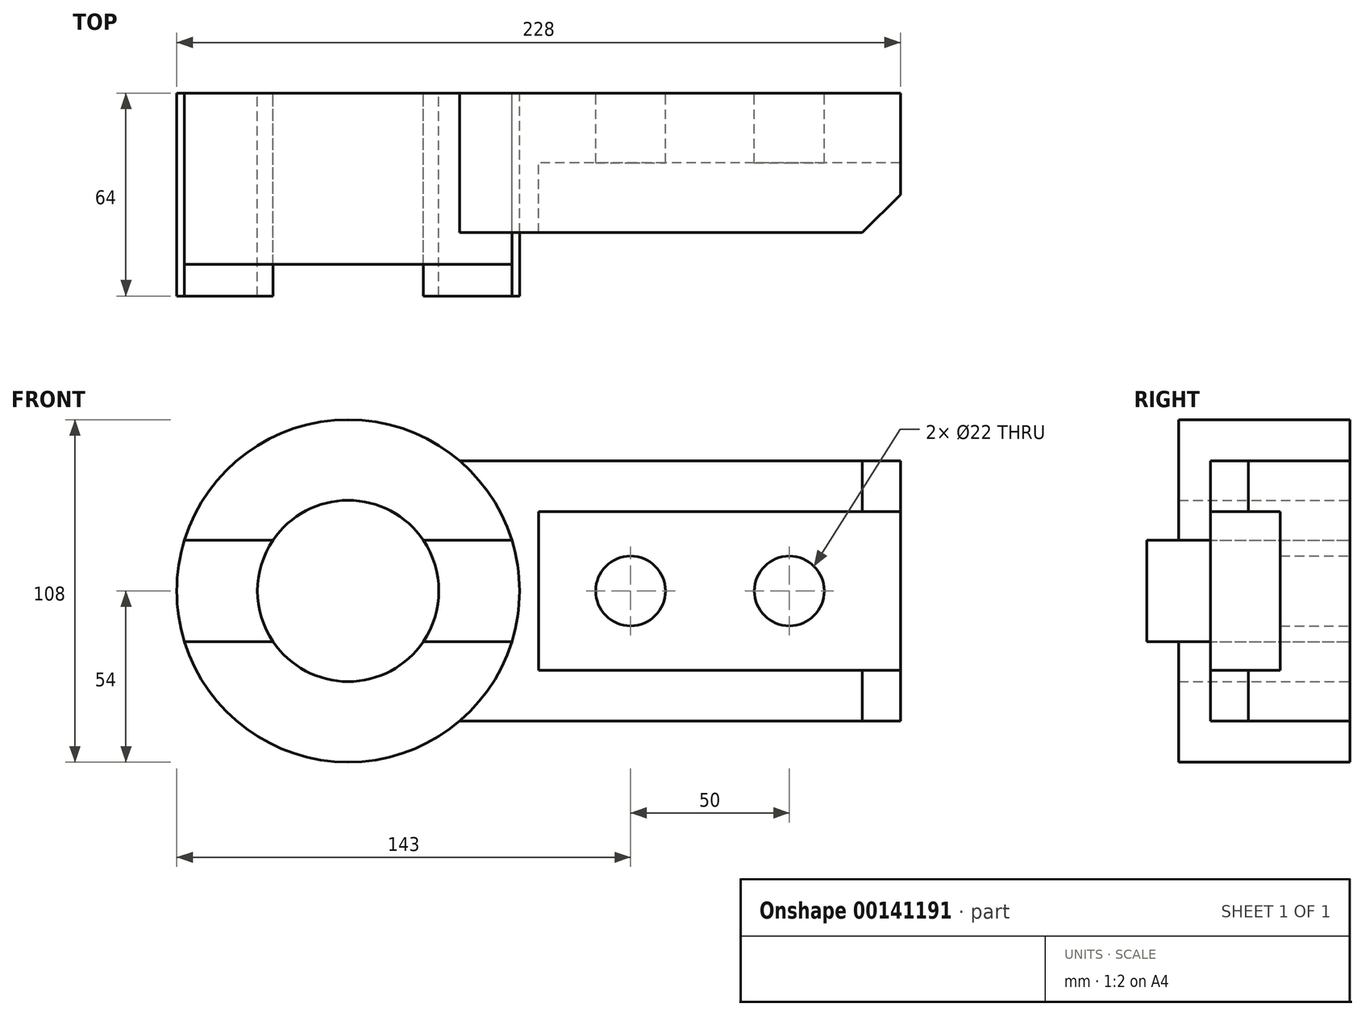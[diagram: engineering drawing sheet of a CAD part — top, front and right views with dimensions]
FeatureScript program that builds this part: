
annotation { "Feature Type Name" : "Feature", "Feature Type Description" : "" }
export const myFeature = defineFeature(function(context is Context, id is Id, definition is map)
    precondition{}
    {
        {
            var Q0;
            Q0=qCreatedBy(makeId("Front.planeOp"),FACE);
            var sketch = newSketch(context, id + "F0", { "sketchPlane" : qUnion([Q0])});
            skCircle(sketch, "E0", {"center": v(0, 0) * mm, "radius": 54 * mm});
            skLineSegment(sketch, "E1", {"start": v(35.14, 41) * mm, "end": v(174, 41) * mm});
            skLineSegment(sketch, "E2.MirrorCS", {"start": v(35.14, -41) * mm, "end": v(174, -41) * mm});
            skLineSegment(sketch, "E3", {"start": v(174, 41) * mm, "end": v(174, -41) * mm});
            skLineSegment(sketch, "E4", {"start": v(174, 25) * mm, "end": v(60, 25) * mm});
            skLineSegment(sketch, "E5.MirrorCS", {"start": v(174, -25) * mm, "end": v(60, -25) * mm});
            skLineSegment(sketch, "E6", {"start": v(60, 25) * mm, "end": v(60, -25) * mm});
            skCircle(sketch, "E7", {"center": v(89, 0) * mm, "radius": 11 * mm});
            skCircle(sketch, "E8", {"center": v(139, 0) * mm, "radius": 11 * mm});
            skCircle(sketch, "E9", {"center": v(0, 0) * mm, "radius": 28.57 * mm});
            skLineSegment(sketch, "E10", {"start": v(-51.58, 16) * mm, "end": v(-23.68, 16) * mm});
            skLineSegment(sketch, "E11", {"start": v(23.68, 16) * mm, "end": v(51.58, 16) * mm});
            skLineSegment(sketch, "E12.MirrorCS", {"start": v(-51.58, -16) * mm, "end": v(-23.68, -16) * mm});
            skLineSegment(sketch, "E13.MirrorCS", {"start": v(23.68, -16) * mm, "end": v(51.58, -16) * mm});
            skSolve(sketch);
        }
        {
            var Q0;
            {var subQ0=sQuery(id+"F0.wireOp",EDGE,"E10");Q0=makeQuery(id+"F0.imprint","IMPRINT",FACE,{"disambiguationData":[TD([[makeQuery(id+"F0.imprint","IMPRINT",EDGE,{"derivedFrom":subQ0}),1.0]])]});}
            var Q1;
            {var subQ0=sQuery(id+"F0.wireOp",EDGE,"E12.MirrorCS");Q1=makeQuery(id+"F0.imprint","IMPRINT",FACE,{"disambiguationData":[TD([[makeQuery(id+"F0.imprint","IMPRINT",EDGE,{"derivedFrom":subQ0}),-1.0]])]});}
            extrude(context, id + "F1", {"entities" : qUnion([Q0, Q1]), "depth" : 54 * mm});
        }
        {
            var Q0;
            {var subQ0=sQuery(id+"F0.wireOp",EDGE,"E10");Q0=makeQuery(id+"F0.imprint","IMPRINT",FACE,{"disambiguationData":[TD([[makeQuery(id+"F0.imprint","IMPRINT",EDGE,{"derivedFrom":subQ0}),-1.0]])]});}
            var Q1;
            {var subQ0=sQuery(id+"F0.wireOp",EDGE,"E11");Q1=makeQuery(id+"F0.imprint","IMPRINT",FACE,{"disambiguationData":[TD([[makeQuery(id+"F0.imprint","IMPRINT",EDGE,{"derivedFrom":subQ0}),-1.0]])]});}
            extrude(context, id + "F2", {"entities" : qUnion([Q0, Q1]), "depth" : 64 * mm});
        }
        {
            var Q0;
            {var subQ0=sQuery(id+"F0.wireOp",EDGE,"E1");Q0=makeQuery(id+"F0.imprint","IMPRINT",FACE,{"disambiguationData":[TD([[makeQuery(id+"F0.imprint","IMPRINT",EDGE,{"derivedFrom":subQ0}),-1.0]])]});}
            extrude(context, id + "F3", {"entities" : qUnion([Q0]), "depth" : 44 * mm});
        }
        {
            var Q0;
            {var subQ1=sQuery(id+"F0.wireOp",EDGE,"E4");Q0=makeQuery(id+"F0.imprint","IMPRINT",FACE,{"disambiguationData":[TD([[makeQuery(id+"F0.imprint","IMPRINT",EDGE,{"derivedFrom":subQ1}),1.0]])]});}
            extrude(context, id + "F4", {"entities" : qUnion([Q0]), "operationType" : NewBodyOperationType.ADD, "depth" : 22 * mm});
        }
        {
            var Q0;
            Q0=makeQuery(id+"F3.opExtrude","SWEPT_FACE",FACE,{"disambiguationData":[OSD([sQuery(id+"F0.wireOp",EDGE,"E2.MirrorCS")])]});
            var sketch = newSketch(context, id + "F5", { "sketchPlane" : qUnion([Q0])});
            skLineSegment(sketch, "E14", {"start": v(35.14, 44) * mm, "end": v(202.33, 44) * mm, "construction": true});
            skLineSegment(sketch, "E15", {"start": v(162, 44) * mm, "end": v(174, 32) * mm});
            skSolve(sketch);
        }
        {
            var Q0;
            {var subQ0=sQuery(id+"F5.wireOp",EDGE,"E15");Q0=makeQuery(id+"F5.imprint","IMPRINT",FACE,{"disambiguationData":[TD([[makeQuery(id+"F5.imprint","IMPRINT",EDGE,{"derivedFrom":subQ0}),1.0]])]});}
            extrude(context, id + "F6", {"entities" : qUnion([Q0]), "operationType" : NewBodyOperationType.REMOVE, "endBound" : BoundingType.THROUGH_ALL, "oppositeDirection" : true, "depth" : 25 * mm});
        }
    });
